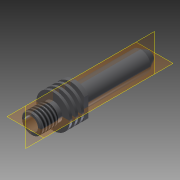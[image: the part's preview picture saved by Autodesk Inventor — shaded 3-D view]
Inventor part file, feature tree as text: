
AUTODESK INVENTOR PART (.ipt)
format: ipt  version: 2015 (Build 190159000, 159)  size: 196,096 bytes
history: native  units: mm
features: extrude x3, plane x3, reference x3, revolve x2, thread x2, chamfer x2, mirror x1
ambient origin geometry x8: Origin, YZ Plane, XZ Plane, XY Plane, X Axis, Y Axis, Z Axis, Center Point
bodies: Solid1 (feature_tree)
feature tree (16):
  revolve  "Revolución1"  [1 undecoded]
  thread  "Rosca1"  [1 undecoded]
  chamfer  "Chaflán1"  Distance=4.0mm
  chamfer  "Chaflán4"  Angle=90.0deg  [1 undecoded]
  extrude  "Extrusión5"  Depth=10.0mm
  thread  "Rosca3"  [1 undecoded]
  extrude  "Extrusión2"  Depth=5.5mm
  plane  "Plano de trabajo1"
  plane  "Plano de trabajo2"
  revolve  "Revolución2"  [1 undecoded]
  plane  "Plano de trabajo3"
  extrude  "Extrusión4"  TaperAngle=45.0deg  [1 undecoded]
  mirror  "Simetría1"
  reference  "Referencia1"
  reference  "Referencia2"
  reference  "Referencia4"
note: 6 required parameter values undecoded (feature->parameter linkage not recoverable at this tier; creation-order binding heuristic only, values carry confidence <= 0.55)